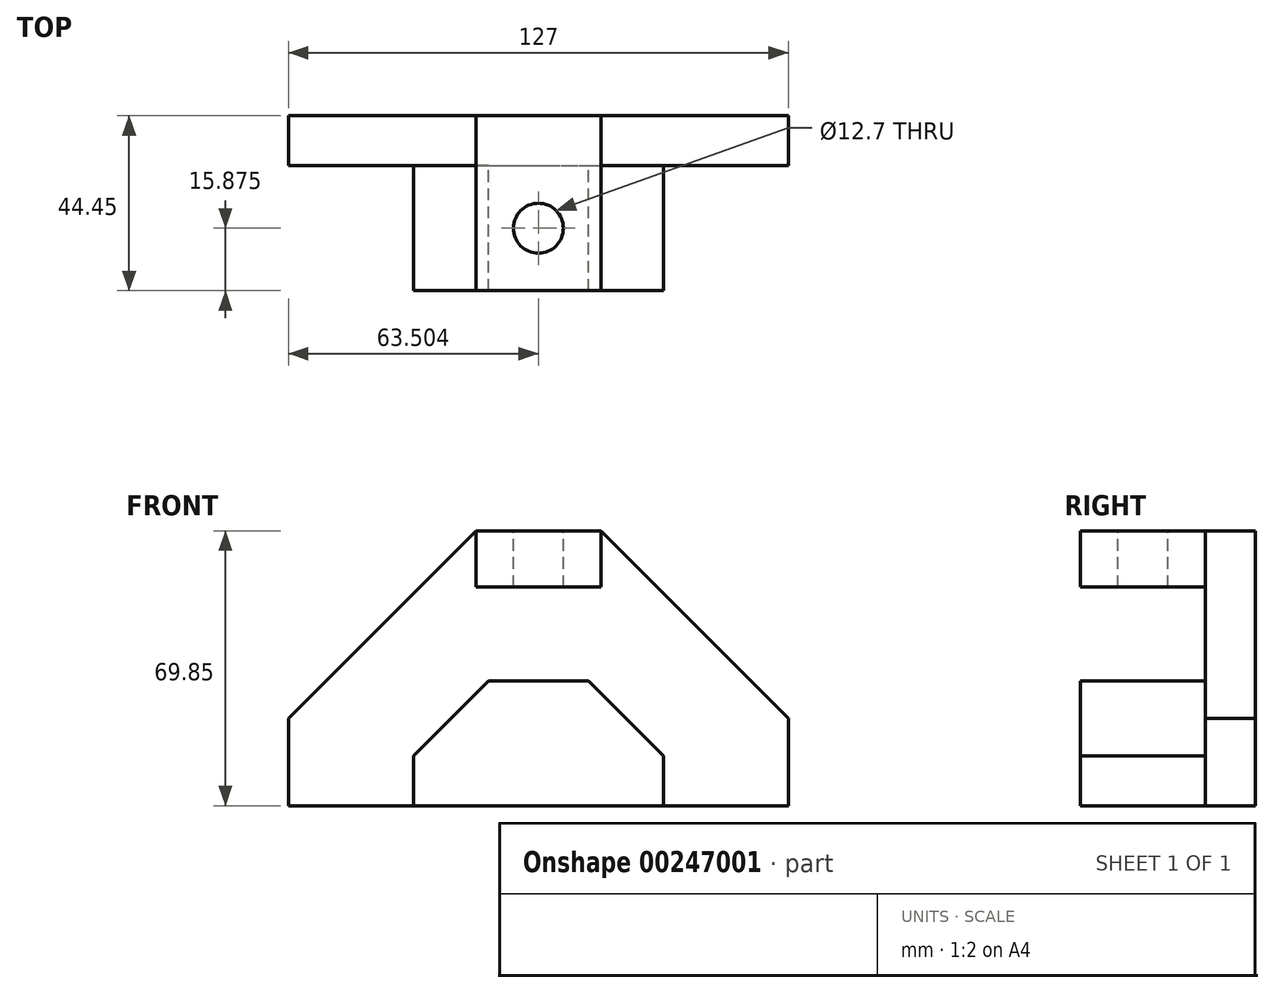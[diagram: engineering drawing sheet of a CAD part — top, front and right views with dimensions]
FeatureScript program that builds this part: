
annotation { "Feature Type Name" : "Feature", "Feature Type Description" : "" }
export const myFeature = defineFeature(function(context is Context, id is Id, definition is map)
    precondition{}
    {
        {
            var Q0;
            Q0=qCreatedBy(makeId("Front.planeOp"),FACE);
            var sketch = newSketch(context, id + "F0", { "sketchPlane" : qUnion([Q0])});
            skLineSegment(sketch, "E0.bottom", {"start": v(-68.86, 17.02) * mm, "end": v(58.14, 17.02) * mm});
            skLineSegment(sketch, "E0.top", {"start": v(-68.86, -52.83) * mm, "end": v(58.14, -52.83) * mm});
            skLineSegment(sketch, "E0.left", {"start": v(-68.86, 17.02) * mm, "end": v(-68.86, -52.83) * mm});
            skLineSegment(sketch, "E0.right", {"start": v(58.14, 17.02) * mm, "end": v(58.14, -52.83) * mm});
            skLineSegment(sketch, "E1", {"start": v(10.52, 17.02) * mm, "end": v(58.14, -30.6) * mm});
            skLineSegment(sketch, "E2", {"start": v(-68.86, -30.6) * mm, "end": v(-21.23, 17.02) * mm});
            skSolve(sketch);
        }
        {
            var Q0;
            {var subQ1=sQuery(id+"F0.wireOp",EDGE,"E0.top");Q0=makeQuery(id+"F0.imprint","IMPRINT",FACE,{"disambiguationData":[TD([[makeQuery(id+"F0.imprint","IMPRINT",EDGE,{"derivedFrom":subQ1}),1.0]])]});}
            extrude(context, id + "F1", {"entities" : qUnion([Q0]), "depth" : 12.7 * mm});
        }
        {
            var Q0;
            Q0=makeQuery(id+"F1.opExtrude","CAP_FACE",FACE,{"disambiguationData":[OSD([sQuery(id+"F0.wireOp",EDGE,"E0.bottom"),sQuery(id+"F0.wireOp",EDGE,"E0.top"),sQuery(id+"F0.wireOp",EDGE,"E0.left"),sQuery(id+"F0.wireOp",EDGE,"E0.right"),sQuery(id+"F0.wireOp",EDGE,"E1"),sQuery(id+"F0.wireOp",EDGE,"E2")])],"isStart":false});
            var sketch = newSketch(context, id + "F2", { "sketchPlane" : qUnion([Q0])});
            skLineSegment(sketch, "E3.bottom", {"start": v(-37.1, -21.08) * mm, "end": v(26.4, -21.08) * mm});
            skLineSegment(sketch, "E3.top", {"start": v(-37.1, -52.83) * mm, "end": v(26.4, -52.83) * mm});
            skLineSegment(sketch, "E3.left", {"start": v(-37.1, -21.08) * mm, "end": v(-37.1, -52.83) * mm});
            skLineSegment(sketch, "E3.right", {"start": v(26.4, -21.08) * mm, "end": v(26.4, -52.83) * mm});
            skLineSegment(sketch, "E4", {"start": v(-18.06, -21.08) * mm, "end": v(-37.1, -40.13) * mm});
            skLineSegment(sketch, "E5", {"start": v(7.34, -21.08) * mm, "end": v(26.4, -40.13) * mm});
            skLineSegment(sketch, "E6.bottom", {"start": v(-21.23, 17.02) * mm, "end": v(10.52, 17.02) * mm});
            skLineSegment(sketch, "E6.top", {"start": v(-21.23, 2.74) * mm, "end": v(10.52, 2.74) * mm});
            skLineSegment(sketch, "E6.left", {"start": v(-21.23, 17.02) * mm, "end": v(-21.23, 2.74) * mm});
            skLineSegment(sketch, "E6.right", {"start": v(10.52, 17.02) * mm, "end": v(10.52, 2.74) * mm});
            skSolve(sketch);
        }
        {
            var Q0;
            {var subQ1=sQuery(id+"F2.wireOp",EDGE,"E3.top");Q0=makeQuery(id+"F2.imprint","IMPRINT",FACE,{"disambiguationData":[TD([[makeQuery(id+"F2.imprint","IMPRINT",EDGE,{"derivedFrom":subQ1}),1.0]])]});}
            extrude(context, id + "F3", {"entities" : qUnion([Q0]), "operationType" : NewBodyOperationType.ADD, "depth" : 31.75 * mm});
        }
        {
            var Q0;
            Q0=makeQuery(id+"F2.imprint","IMPRINT",FACE,{"disambiguationData":[TD([[makeQuery(id+"F2.imprint","IMPRINT",EDGE,{"derivedFrom":sQuery(id+"F2.wireOp",EDGE,"E6.bottom")}),-1.0]])]});
            extrude(context, id + "F4", {"entities" : qUnion([Q0]), "operationType" : NewBodyOperationType.ADD, "depth" : 31.75 * mm});
        }
        {
            var Q0;
            Q0=makeQuery(id+"F4.boolean.opBoolean","MERGE",FACE,{"derivedFrom":[makeQuery(id+"F1.opExtrude","SWEPT_FACE",FACE,{"disambiguationData":[OSD([sQuery(id+"F0.wireOp",EDGE,"E0.bottom")])]}),makeQuery(id+"F4.opExtrude","SWEPT_FACE",FACE,{"disambiguationData":[OSD([sQuery(id+"F2.wireOp",EDGE,"E6.bottom")])]})]});
            var sketch = newSketch(context, id + "F5", { "sketchPlane" : qUnion([Q0])});
            skCircle(sketch, "E7", {"center": v(-5.36, -28.58) * mm, "radius": 6.35 * mm});
            skSolve(sketch);
        }
        {
            var Q0;
            Q0=makeQuery(id+"F5.imprint","IMPRINT",FACE,{"disambiguationData":[TD([[makeQuery(id+"F5.imprint","IMPRINT",EDGE,{"derivedFrom":sQuery(id+"F5.wireOp",EDGE,"E7")}),1.0]])]});
            extrude(context, id + "F6", {"entities" : qUnion([Q0]), "operationType" : NewBodyOperationType.REMOVE, "oppositeDirection" : true, "depth" : 14.29 * mm});
        }
    });
